# Revit family: Argonaut-PLUS_ARGOPLUS-600-xx-LyPOD-zz_Non-Hosted_R16
name_source: partatom
category: Lighting Fixtures
revit_build: Autodesk Revit 2016 (Build: 20151007_0715(x64)
units: mm (PartAtom-declared; Revit-internal decimal feet)

## family parameters
Always vertical = Yes
Cut with Voids When Loaded = No
Light Source = Yes
OmniClass Number = 23.80.70.00
OmniClass Title = Lighting
Part Type = Normal
Room Calculation Point = No
Round Connector Dimension = Use Diameter
Shared = No
Work Plane-Based = No

## types (2) — shared parameters
AS2293 Classification = C0=D80 C90=D80
Applicable Standards = AS/NZS3820, CISPR15, AS/NZS2293.3
Battery = 3.3V 5000mAh
Battery Type = Lithium Nanophosphate
Charging Method = Intelligent current limited constant voltage
Color Filter = 16777215
Colour CCT = Switchable 3000K / 4000K (Default) / 5700K
Construction = Polycarbonate
Diffuser = Polycarbonate
Dimensions (L x W x H) = 720x160x105
Dimming Lamp Color Temperature Shift = <None>
Emergency Lumen Output = 376.3 lm
Emit Shape Visible in Rendering = No
IK Rating = IK08
IP Rating = IP65
Lamp = LED strip module, 3000K / 5700K, Ra>80
L70/B50 Ta 40ºC; LM80 Report >60,000hr, Projected 157,000hr
L80/B20 Ta 40ºC; LM80 Report >60,000hr, Projected 95,000hr
L90/B10 Ta 40ºC; LM80 Report 43,000hr, Projected 43,000hr
Manufacturer = Clevertronics
Mounting = Surface Mount
Operating Mode = Sustained
Operating Temperature = 0ºC to 40ºC
Operating Voltage = 220-240V~ 50Hz
Photometric Web File = ARGOPLUS-600-SEN-LPPOD-HVG_IESR_E_202101291419.ies
Power Consumption (Standby - Lamp Off) = 0.4W
Replacement Battery = 1530050 - BATTERY:L10 3.3V 2.5AH 70mm lead, no Brkt
Replacement Emergency Driver = AUM01370120001 - Lifelight Pro,Control Only,Batten,L10, CTP, OWC,NP
Replacement Emergency Lamp = 8050205 - HWSUB: CT10570-A4 - 2 LED WHITE
Replacement lamp = 8002751 - PCA:LED Strip ARGOPLUS-600,8P8S,3000K/5700K
Testing System = Clevertest Plus Enabled (not activated by default)
Tilt Angle = 90.00°
Weight = 2.0 kg

## per-type parameters (varying)
| type | Description | Earth Leakage | Inrush Current (Max) | LED Driver | MIC Number | Power Consumption (Max Charge Lamp On) | Power Consumption (Standby - Lamp 10%) Sensor Only | Power Consumption (Standby - Lamp On) | Power Factor | Replacement Driver | Sensor | Sensor Capability | Supply Current | Total Lumen Output |
| ARGOPLUS-600-DD-L10POD | Argonaut Plus 600mm Weatherproof Emergency Batten, L10 with POD, Switchable Colour, DALI Driver, Clevertest Plus | 0.5mA | 46.2A<500μs | LED DALI Driver - 25W, 350-1050mA, 20-50V, one4all | AUB01320320001 | 20.0W |  | 17.7W | 0.86 @ default | 1330038 - LED DALI Driver - 25W, 350-1050mA, 20-50V, one4all |  |  | 105mA +/-20mA | 2351 lm (133 lm/W) @ default |
| ARGOPLUS-600-SEN-L10POD | Argonaut Plus 600mm Weatherproof Emergency Batten, L10 with POD, Switchable Colour, Motion Sensor, Clevertest Plus | 0.4mA | 23.23A<800μs | LED Driver - 20W Stallion, MS-HL | AUB01320340001 | 21.3W | 2.9W | 19.0W | 0.85 @ default | 1330087 - LED Driver - 20W Stallion, MS-HL | 1190132 - SENSOR: Head Only, t/s Stallion | High/Low, Master Slave - No | 107mA +/-20mA | 2351 lm (128 lm/W) @ default |

note: column(s) folded — value = type name in every type: Model

## geometry (parser evidence)
native form markers: Sweep x2
no freeform markers — native parametric forms only
